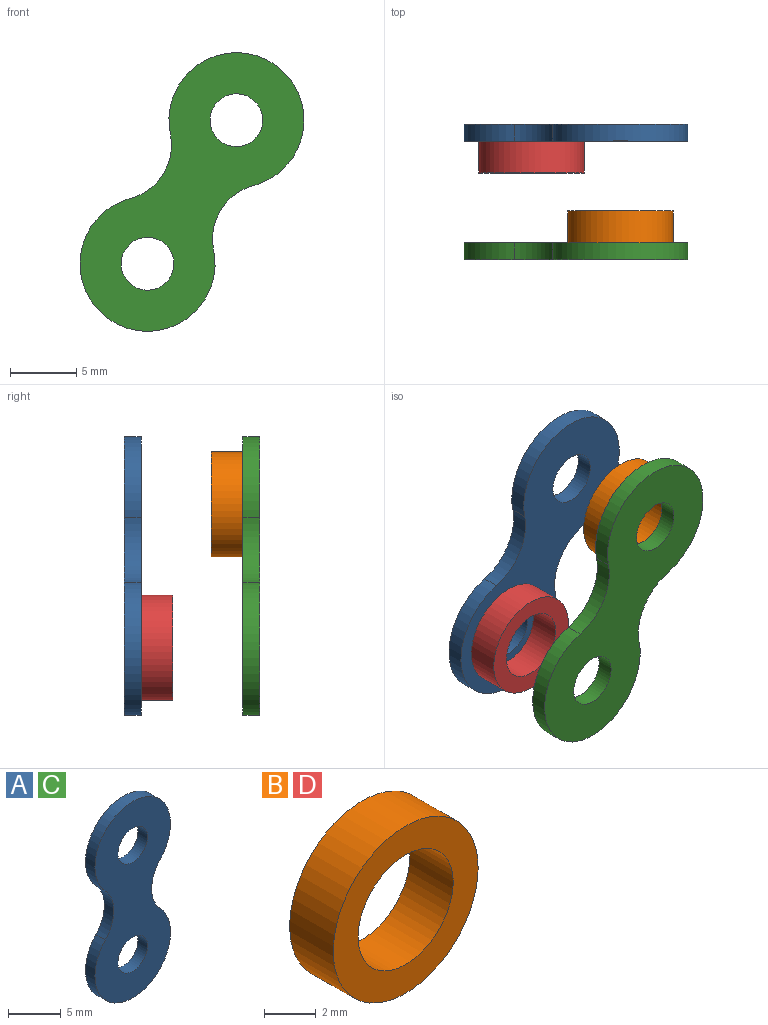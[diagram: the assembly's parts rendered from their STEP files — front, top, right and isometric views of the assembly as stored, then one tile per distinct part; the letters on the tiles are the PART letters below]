
ASSEMBLY  parts=4 mates=2
PART A: 8 faces, bbox 10.2x1.3x22.9 mm
  f0: cylinder r=4.15mm len=5.71mm, axis (0,1,0), area 8mm2, adj f1,f5,f6,f7
  f1: cylinder r=5.08mm len=10.16mm, axis (0,1,0), area 30.1mm2, adj f0,f2,f6,f7
  f2: cylinder r=4.15mm len=5.71mm, axis (0,1,0), area 8mm2, adj f1,f5,f6,f7
  f3: cylinder r=1.98mm len=3.97mm, axis (0,1,0), area 15.8mm2, adj f6,f7
  f4: cylinder r=1.98mm len=3.97mm, axis (0,1,0), area 15.8mm2, adj f6,f7
  f5: cylinder r=5.08mm len=10.16mm, axis (0,1,0), area 30.1mm2, adj f0,f2,f6,f7
  f6: plane 22.86x10.16mm, normal (0,-1,0), area 154.4mm2, adj f0,f1,f2,f3,f4,f5
  f7: plane 22.86x10.16mm, normal (0,1,0), area 154.4mm2, adj f0,f1,f2,f3,f4,f5
PART B: 4 faces, bbox 7.9x2.4x7.9 mm
  f0: cylinder r=2.6mm len=5.21mm, axis (0,1,0), area 39mm2, adj f2,f3
  f1: cylinder r=3.97mm len=7.94mm, axis (0,1,0), area 59.4mm2, adj f2,f3
  f2: plane 7.94x7.94mm, normal (0,-1,0), area 28.2mm2, adj f0,f1
  f3: plane 7.94x7.94mm, normal (0,1,0), area 28.2mm2, adj f0,f1
PART C: same geometry as A
PART D: same geometry as B
PLACE A rot(axis=(0,1,0),31.8deg) t=(42.85,19.27,4.99)mm
PLACE B rot(axis=(0,1,0),31.8deg) t=(42.85,12.75,4.99)mm
PLACE C rot(axis=(0,1,0),31.8deg) t=(42.85,10.36,4.99)mm
PLACE D rot(axis=(0,-1,0),1.5deg) t=(36.16,18,-5.8)mm
MATE revolute B.f0 <-> C.f3  axis (0,-1,0) through (42.85,10.36,4.99)mm
MATE revolute D.f0 <-> A.f1  axis (0,1,0) through (36.16,18,-5.8)mm
